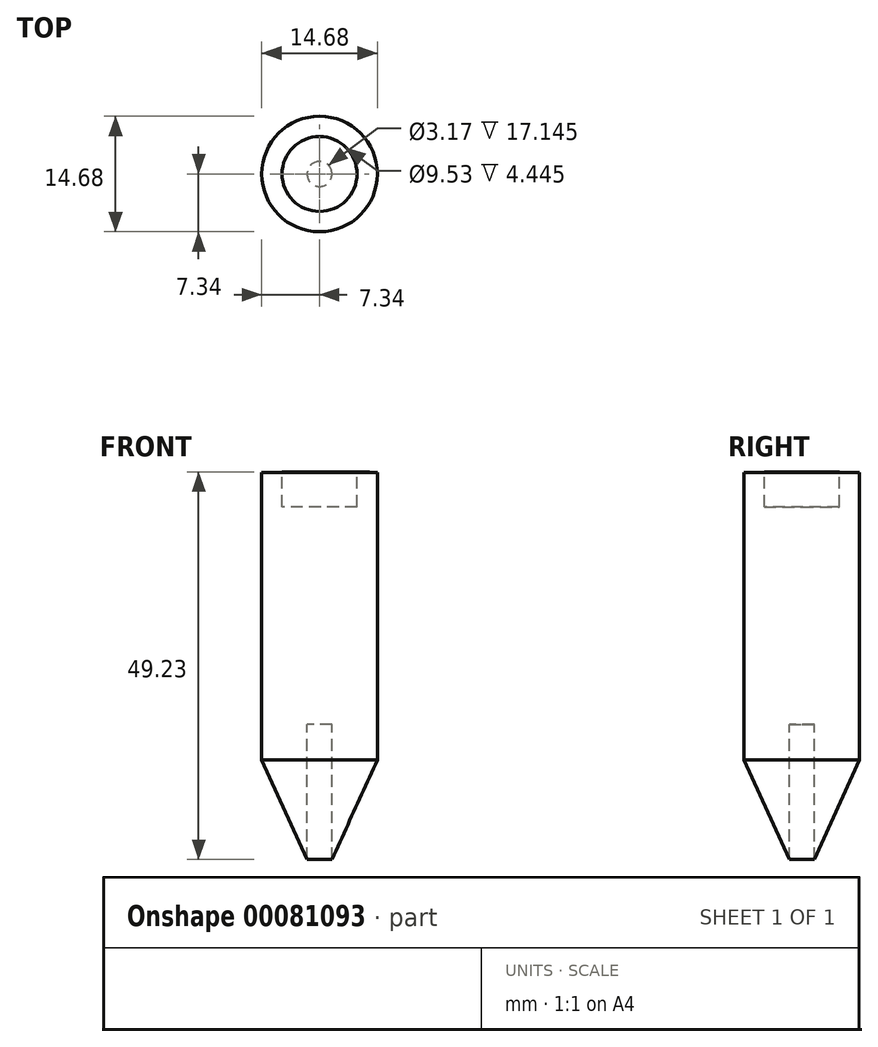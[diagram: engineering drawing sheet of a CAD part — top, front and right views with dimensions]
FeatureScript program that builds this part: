
annotation { "Feature Type Name" : "Feature", "Feature Type Description" : "" }
export const myFeature = defineFeature(function(context is Context, id is Id, definition is map)
    precondition{}
    {
        {
            var Q0;
            Q0=qCreatedBy(makeId("Front.planeOp"),FACE);
            var sketch = newSketch(context, id + "F0", { "sketchPlane" : qUnion([Q0])});
            skLineSegment(sketch, "E0.bottom", {"start": v(0, -40.83) * mm, "end": v(1.59, -40.83) * mm});
            skLineSegment(sketch, "E0.top", {"start": v(0, -23.68) * mm, "end": v(1.59, -23.68) * mm});
            skLineSegment(sketch, "E0.left", {"start": v(0, -40.83) * mm, "end": v(0, -23.68) * mm});
            skLineSegment(sketch, "E0.right", {"start": v(1.59, -40.83) * mm, "end": v(1.59, -23.68) * mm});
            skLineSegment(sketch, "E1", {"start": v(1.59, -40.83) * mm, "end": v(7.34, -28.2) * mm});
            skPoint(sketch, "E2.left.start.orphan", {"position": v(0, 8.4) * mm});
            skLineSegment(sketch, "E3.bottom", {"start": v(0, 8.4) * mm, "end": v(4.76, 8.4) * mm});
            skLineSegment(sketch, "E3.top", {"start": v(0, 3.96) * mm, "end": v(4.76, 3.96) * mm});
            skLineSegment(sketch, "E3.left", {"start": v(0, 8.4) * mm, "end": v(0, 3.96) * mm});
            skLineSegment(sketch, "E3.right", {"start": v(4.76, 8.4) * mm, "end": v(4.76, 3.96) * mm});
            skLineSegment(sketch, "E4", {"start": v(4.76, 8.4) * mm, "end": v(7.34, 8.3) * mm});
            skLineSegment(sketch, "E5", {"start": v(0, 3.96) * mm, "end": v(0, -23.68) * mm});
            skPoint(sketch, "E6.end.orphan", {"position": v(5.41, 0) * mm});
            skLineSegment(sketch, "E7", {"start": v(16.83, 0) * mm, "end": v(15.13, 0) * mm});
            skLineSegment(sketch, "E8", {"start": v(7.34, 8.3) * mm, "end": v(7.34, 0) * mm});
            skLineSegment(sketch, "E9", {"start": v(7.34, 0) * mm, "end": v(8.25, 0) * mm});
            skPoint(sketch, "E10.start.orphan", {"position": v(4.76, 0) * mm});
            skPoint(sketch, "E11.endSnap0", {"position": v(12.08, -24.26) * mm});
            skPoint(sketch, "E12.end.orphan", {"position": v(15.13, 0) * mm});
            skPoint(sketch, "E13.orphan", {"position": v(16.83, -20.3) * mm});
            skPoint(sketch, "E14.start.orphan", {"position": v(12.08, -23.68) * mm});
            skLineSegment(sketch, "E15", {"start": v(7.34, 0) * mm, "end": v(7.34, -28.2) * mm});
            skSolve(sketch);
        }
        {
            var Q0;
            Q0=makeQuery(id+"F0.imprint","IMPRINT",FACE,{"disambiguationData":[TD([[makeQuery(id+"F0.imprint","IMPRINT",EDGE,{"derivedFrom":sQuery(id+"F0.wireOp",EDGE,"E0.top")}),1.0]])]});
            var Q1;
            Q1=sQuery(id+"F0.wireOp",EDGE,"E5");
            revolve(context, id + "F1", {"entities" : qUnion([Q0]), "axis" : qUnion([Q1]), "revolveType" : RevolveType.FULL});
        }
    });
